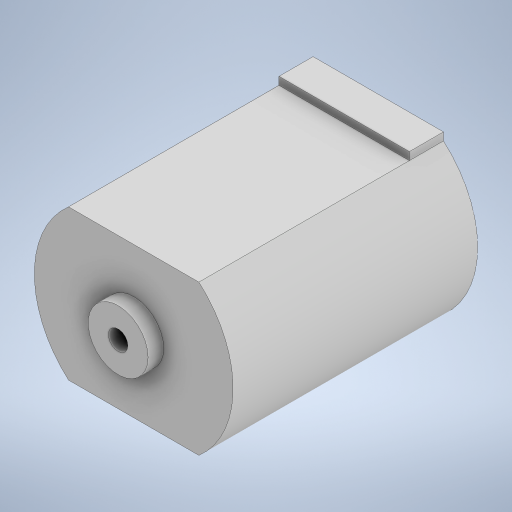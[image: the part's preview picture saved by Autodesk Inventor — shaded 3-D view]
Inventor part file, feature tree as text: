
AUTODESK INVENTOR PART (.ipt)
format: ipt  version: 2023 (Build 270158000, 158)  size: 248,320 bytes
history: native  units: in
note: dims shown in document units (in); Inventor stores cm internally (conversion verified against a paired STEP export)
features: extrude x5, sketch x4, plane x1
ambient origin geometry x8: Origin, YZ Plane, XZ Plane, XY Plane, X Axis, Y Axis, Z Axis, Center Point
bodies: Solid1 (feature_tree)
feature tree (10):
  extrude  "Extrusion1"  Depth=0.9882in TaperAngle=0.0deg
  plane  "Work Plane1"
  extrude  "Extrusion2"  Depth=0.3031in
  extrude  "Extrusion3"  Depth=0.3031in TaperAngle=0.0deg
  extrude  "Extrusion4"  Depth=0.063in
  extrude  "Extrusion6"  Depth=0.063in TaperAngle=0.0deg
  sketch  "Sketch1"  dims[d0=0.8031in d1=0.9882in d2=0.0in]
  sketch  "Sketch3"  dims[d3=0.0in d4=0.3031in]
  sketch  "Sketch4"  dims[d5=0.3031in d6=0.8661in d7=0.0in]
  sketch  "Sketch5"  dims[d8=0.2421in d9=0.0787in d10=0.063in d11=0.0in d12=0.1378in d13=0.0315in d14=0.0in d15=0.374in d18=0.063in d19=0.0in d20=0.0197in d21=0.0344in]
